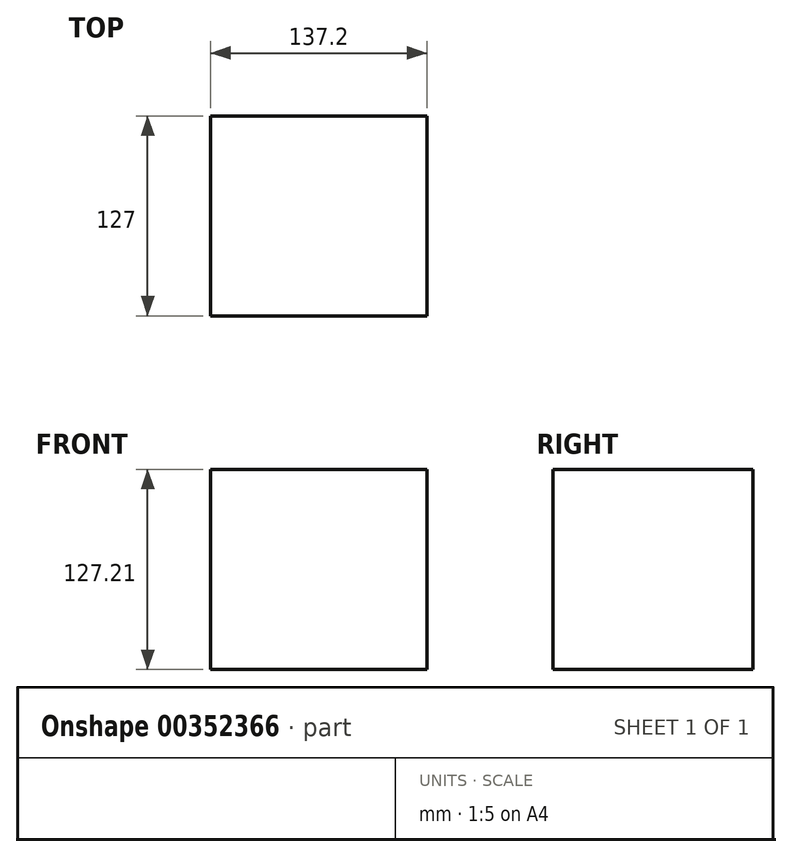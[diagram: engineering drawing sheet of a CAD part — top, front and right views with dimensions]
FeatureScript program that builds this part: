
annotation { "Feature Type Name" : "Feature", "Feature Type Description" : "" }
export const myFeature = defineFeature(function(context is Context, id is Id, definition is map)
    precondition{}
    {
        {
            var Q0;
            Q0=qCreatedBy(makeId("Front.planeOp"),FACE);
            var sketch = newSketch(context, id + "F0", { "sketchPlane" : qUnion([Q0])});
            skLineSegment(sketch, "E0.bottom", {"start": v(-76.14, 0) * mm, "end": v(61.06, 0) * mm});
            skLineSegment(sketch, "E0.top", {"start": v(-76.14, 127.21) * mm, "end": v(61.06, 127.21) * mm});
            skLineSegment(sketch, "E0.left", {"start": v(-76.14, 0) * mm, "end": v(-76.14, 127.21) * mm});
            skLineSegment(sketch, "E0.right", {"start": v(61.06, 0) * mm, "end": v(61.06, 127.21) * mm});
            skSolve(sketch);
        }
        {
            var Q0;
            Q0=makeQuery(id+"F0.imprint","IMPRINT",FACE,{"disambiguationData":[TD([[makeQuery(id+"F0.imprint","IMPRINT",EDGE,{"derivedFrom":sQuery(id+"F0.wireOp",EDGE,"E0.bottom")}),1.0]])]});
            extrude(context, id + "F1", {"entities" : qUnion([Q0]), "depth" : 127 * mm});
        }
    });
